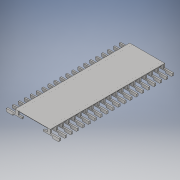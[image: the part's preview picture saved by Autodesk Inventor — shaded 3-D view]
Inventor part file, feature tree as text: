
AUTODESK INVENTOR PART (.ipt)
format: ipt  version: 2019 (Build 230136000, 136)  size: 612,352 bytes
history: native  units: in
note: dims shown in document units (in); Inventor stores cm internally (conversion verified against a paired STEP export)
features: other x14, extrude x3, sketch x3
ambient origin geometry x8: Origin, YZ Plane, XZ Plane, XY Plane, X Axis, Y Axis, Z Axis, Center Point
bodies: Solid1 (feature_tree)
feature tree (20):
  extrude  "Extrusion1"  Depth=2.0in TaperAngle=0.0deg
  extrude  "Extrusion2"  [1 undecoded]
  extrude  "Extrusion3"  [1 undecoded]
  other  "p1_to_p2_XY"
  other  "p1_to_p2_YZ"
  other  "p1_to_p2_ZX"
  other  "p1_to_p2_X"
  other  "p1_to_p2_Y"
  other  "p1_to_p2_Z"
  other  "p1_to_p2_Center"
  other  "pin_XY"
  other  "pin_YZ"
  other  "pin_ZX"
  other  "pin_X"
  other  "pin_Y"
  other  "pin_Z"
  other  "pin_Center"
  sketch  "Sketch_1"  dims[d0=0.61in d1=0.0in d2=2.0in d3=0.0in]
  sketch  "Sketch_2"  dims[d4=100.0in d5=0.0in]
  sketch  "Sketch_5"
note: 2 required parameter values undecoded (feature->parameter linkage not recoverable at this tier; creation-order binding heuristic only, values carry confidence <= 0.55)
